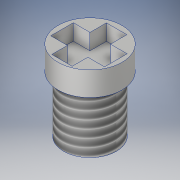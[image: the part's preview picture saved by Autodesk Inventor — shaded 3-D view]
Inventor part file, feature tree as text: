
AUTODESK INVENTOR PART (.ipt)
format: ipt  version: 2018 (Build 220112000, 112)  size: 135,168 bytes
history: native  units: in
note: dims shown in document units (in); Inventor stores cm internally (conversion verified against a paired STEP export)
features: sketch x2, revolve x1, thread x1, extrude x1
ambient origin geometry x8: Origin, YZ Plane, XZ Plane, XY Plane, X Axis, Y Axis, Z Axis, Center Point
bodies: Solid1 (feature_tree)
feature tree (5):
  revolve  "Revolution1"  [1 undecoded]
  thread  "Thread1"  [1 undecoded]
  extrude  "Extrusion1"  TaperAngle=90.0deg  [1 undecoded]
  sketch  "Sketch1"  dims[d0=0.1in d1=0.075in d2=0.0175in]
  sketch  "Sketch2"  dims[d3=0.175in d4=90.0deg d5=1.0in d6=0.0in d7=0.05in d8=0.0in]
note: 3 required parameter values undecoded (feature->parameter linkage not recoverable at this tier; creation-order binding heuristic only, values carry confidence <= 0.55)